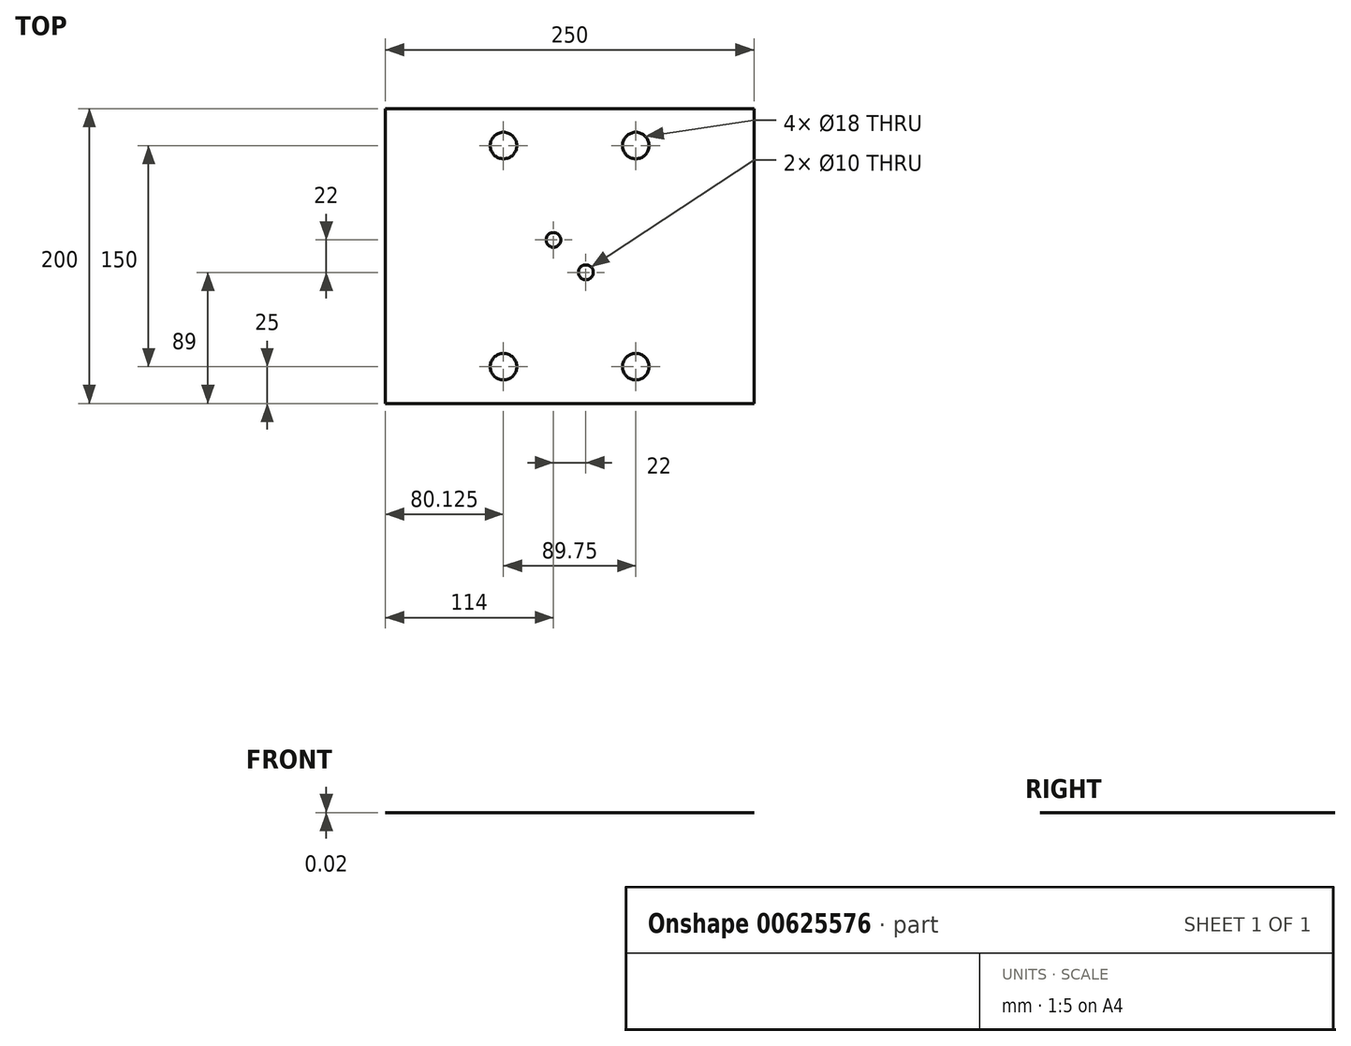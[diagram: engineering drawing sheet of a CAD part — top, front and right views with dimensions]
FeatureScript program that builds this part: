
annotation { "Feature Type Name" : "Feature", "Feature Type Description" : "" }
export const myFeature = defineFeature(function(context is Context, id is Id, definition is map)
    precondition{}
    {
        {
            var Q0;
            Q0=qCreatedBy(makeId("Top.planeOp"),FACE);
            var sketch = newSketch(context, id + "F0", { "sketchPlane" : qUnion([Q0])});
            skLineSegment(sketch, "E0.bottom", {"start": v(-125, -100) * mm, "end": v(125, -100) * mm});
            skLineSegment(sketch, "E0.top", {"start": v(-125, 100) * mm, "end": v(125, 100) * mm});
            skLineSegment(sketch, "E0.left", {"start": v(-125, -100) * mm, "end": v(-125, 100) * mm});
            skLineSegment(sketch, "E0.right", {"start": v(125, -100) * mm, "end": v(125, 100) * mm});
            skPoint(sketch, "E0.middle", {"position": v(0, 0) * mm});
            skCircle(sketch, "E1", {"center": v(-44.88, -75) * mm, "radius": 3.56 * mm});
            skCircle(sketch, "E2", {"center": v(-11, 11) * mm, "radius": 2.5 * mm});
            skCircle(sketch, "E3", {"center": v(-44.88, 75) * mm, "radius": 3.56 * mm});
            skCircle(sketch, "E4", {"center": v(11, -11) * mm, "radius": 2.5 * mm});
            skCircle(sketch, "E5", {"center": v(44.88, -75) * mm, "radius": 2.5 * mm});
            skCircle(sketch, "E6", {"center": v(44.88, 75) * mm, "radius": 2.5 * mm});
            skLineSegment(sketch, "E7", {"start": v(-44.88, 75) * mm, "end": v(-44.88, -75) * mm, "construction": true});
            skLineSegment(sketch, "E8", {"start": v(44.88, 75) * mm, "end": v(44.88, -75) * mm, "construction": true});
            skLineSegment(sketch, "E9", {"start": v(-44.88, 75) * mm, "end": v(44.88, 75) * mm, "construction": true});
            skLineSegment(sketch, "E10", {"start": v(-44.88, -75) * mm, "end": v(44.88, -75) * mm, "construction": true});
            skSolve(sketch);
        }
        {
            var Q0;
            Q0 = qSketchRegion(id + "F0", true);
            extrude(context, id + "F1", {"entities" : qUnion([Q0]), "depth" : 1 / 50.8 * mm, "offsetDistance" : 25 * mm});
        }
        {
            var Q0;
            Q0=makeQuery(id+"F1.opExtrude","CAP_FACE",FACE,{"disambiguationData":[OSD([sQuery(id+"F0.wireOp",EDGE,"E0.bottom"),sQuery(id+"F0.wireOp",EDGE,"E0.top"),sQuery(id+"F0.wireOp",EDGE,"E0.left"),sQuery(id+"F0.wireOp",EDGE,"E0.right"),sQuery(id+"F0.wireOp",EDGE,"E1"),sQuery(id+"F0.wireOp",EDGE,"E2"),sQuery(id+"F0.wireOp",EDGE,"E3"),sQuery(id+"F0.wireOp",EDGE,"E4"),sQuery(id+"F0.wireOp",EDGE,"E5"),sQuery(id+"F0.wireOp",EDGE,"E6")])],"isStart":false});
            var sketch = newSketch(context, id + "F2", { "sketchPlane" : qUnion([Q0])});
            skCircle(sketch, "E11", {"center": v(-44.88, 75) * mm, "radius": 9 * mm});
            skCircle(sketch, "E12", {"center": v(44.88, 75) * mm, "radius": 9 * mm});
            skCircle(sketch, "E13", {"center": v(-44.88, -75) * mm, "radius": 9 * mm});
            skCircle(sketch, "E14", {"center": v(44.88, -75) * mm, "radius": 9 * mm});
            skCircle(sketch, "E15", {"center": v(-11, 11) * mm, "radius": 5 * mm});
            skCircle(sketch, "E16", {"center": v(11, -11) * mm, "radius": 5 * mm});
            skSolve(sketch);
        }
        {
            var Q0;
            Q0 = qSketchRegion(id + "F2", true);
            extrude(context, id + "F3", {"entities" : qUnion([Q0]), "operationType" : NewBodyOperationType.REMOVE, "oppositeDirection" : true, "depth" : 6 * mm, "offsetDistance" : 25 * mm});
        }
    });
